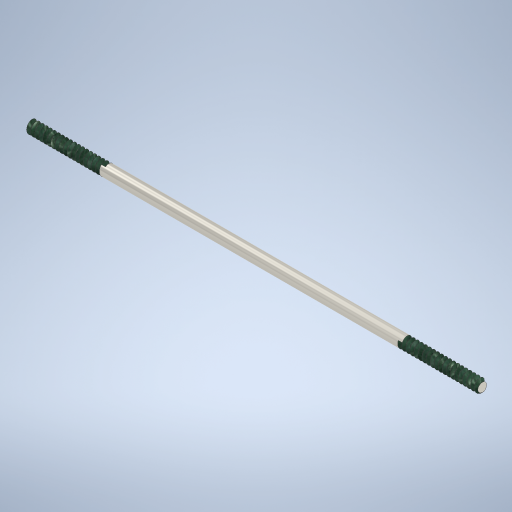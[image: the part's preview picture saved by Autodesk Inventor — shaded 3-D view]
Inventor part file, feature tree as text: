
AUTODESK INVENTOR PART (.ipt)
format: ipt  version: 2024 (Build 280153000, 153)  size: 432,128 bytes
history: native  units: mm
features: sketch x3, helix x2, extrude x1
ambient origin geometry x8: Origin, YZ Plane, XZ Plane, XY Plane, X Axis, Y Axis, Z Axis, Center Point
bodies: Solid1 (feature_tree)
feature tree (6):
  extrude  "Extrusion1"  Depth=1.7mm TaperAngle=0.0deg
  helix  "Coil1"  [1 undecoded]
  helix  "Coil2"  [1 undecoded]
  sketch  "Sketch1"  dims[d0=5.0mm d1=190.0mm d2=0.0mm d3=1.7mm d4=60.0deg]
  sketch  "Sketch2"  dims[d5=0.2mm]
  sketch  "Sketch3"  dims[d6=2.0mm d7=1.7mm d8=35.0mm d9=10.0mm d10=0.0mm d11=90.0deg d12=90.0deg d13=0.0mm d14=0.0mm d15=1.7mm d16=60.0deg d17=0.2mm d18=2.0mm d19=1.7mm d20=35.0mm d21=10.0mm d22=0.0mm d23=90.0deg d24=90.0deg d25=0.0mm d26=0.0mm]
note: 2 required parameter values undecoded (feature->parameter linkage not recoverable at this tier; creation-order binding heuristic only, values carry confidence <= 0.55)
